# Revit family: Reece_Toilet_Roca_Ona_Back to Wall_Rimless
name_source: partatom
category: Plumbing Fixtures
revit_build: Autodesk Revit 2018 (Build: 20181011_1500(x64)
units: mm (PartAtom-declared; Revit-internal decimal feet)

## family parameters
Always vertical = Yes
Cut with Voids When Loaded = Yes
Part Type = Normal
Room Calculation Point = No
Round Connector Dimension = Use Diameter
Shared = No
Work Plane-Based = Yes

## types (1)
- White
    Default Elevation = 0 mm  [stored 0 ft]
    Description = Roca Ona Back To Wall Rimless Pan with Soft Close Quick Release Toilet Seat White (4 Star)
    Disclaimer = THIS FILE IS THE PROPERTY OF THE REECE GROUP. IT MAY NOT BE REPRODUCED, REVERSE-ENGINEERED, OR MODIFIED. ANY REPUBLICATION, TRANSMISSION, OR DISTRIBUTION FOR THE PURPOSE OF COMMERCIALLY EXPLOITING THE FILES IS PROHIBITED.
    Keynote = Product #10049, Reece_Toilet_Roca_Ona_Back to Wall_Rimless - White
    Manufacturer = Roca
    Model = Ona
    Reece_Back_Inlet = 55 mm
    Reece_Back_Outlet_Offset = 180 mm  [stored 0.590551 ft]
    Reece_Bottom_Outlet_Offset = 95 mm
    Reece_Detail_Disclaimer = THIS FILE IS THE PROPERTY OF THE REECE GROUP. IT MAY NOT BE REPRODUCED, REVERSE-ENGINEERED, OR MODIFIED. ANY REPUBLICATION, TRANSMISSION, OR DISTRIBUTION FOR THE PURPOSE OF COMMERCIALLY EXPLOITING THE FILES IS PROHIBITED.
    Reece_Detail_Function = Universal S & P
    Reece_Detail_Installation = Back to Wall
    Reece_Detail_Shape = Rimless
    Reece_Material_Main = Reece_Vitreous China_White
    Reece_Material_Seat = Reece_Plastic_Urea_White
    Reece_Material_Secondary = Reece_Brass_Chrome
    Reece_Overall_Height = 465 mm
    Reece_Overall_Pan_Projection = 530 mm  [stored 1.73885 ft]
    Reece_Overall_Width = 363 mm
    Reece_P_Trap = 102 mm
    Reece_Pan_Height = 420 mm  [stored 1.37795 ft]
    Reece_Pan_Width = 360 mm
    Reece_Product_Brand = Roca
    Reece_Product_Description = Roca Ona Back To Wall Rimless Pan with Soft Close Quick Release Toilet Seat White (4 Star)
    Reece_Product_Mount = Floor Mounted
    Reece_Product_Number = 10049
    Reece_Product_Sub Brand = Ona
    Reece_Product_Type = Toilet
    Reece_Product_Web Page = https://www.reece.com.au
    Reece_S_Trap = 102 mm
    Type Comments = Toilet
    URL = https://www.reece.com.au

note: [stored X ft] marks values corroborated as IEEE doubles in the binary element streams (Revit-internal decimal feet)

## geometry (parser evidence)
native form markers: Sweep x8
no freeform markers — native parametric forms only
